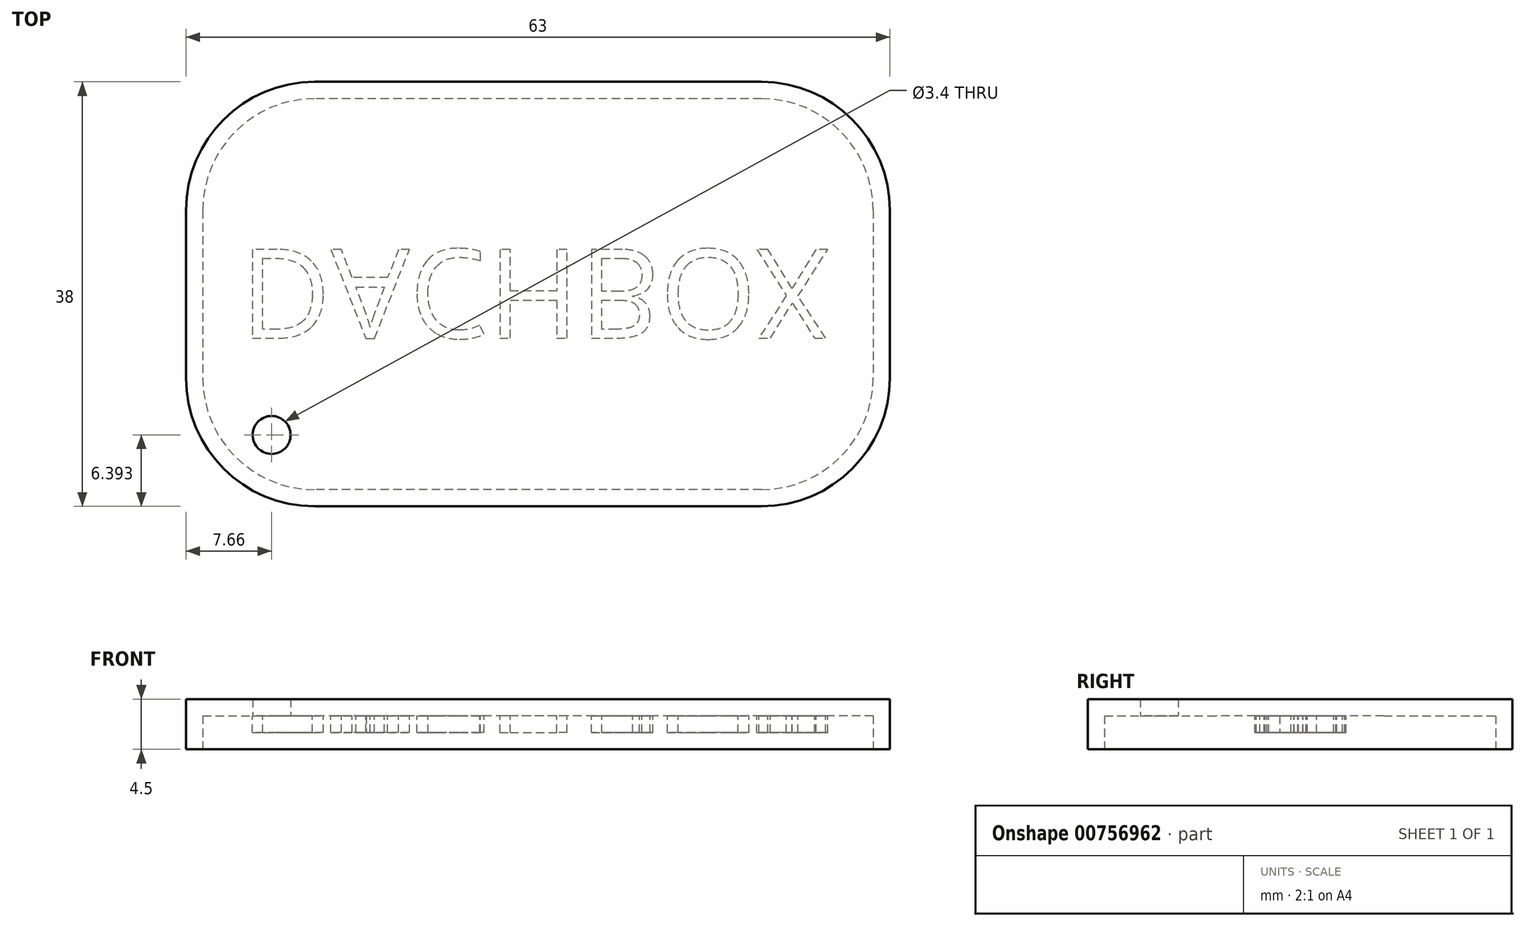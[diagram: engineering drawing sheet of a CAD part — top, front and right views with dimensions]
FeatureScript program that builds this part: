
annotation { "Feature Type Name" : "Feature", "Feature Type Description" : "" }
export const myFeature = defineFeature(function(context is Context, id is Id, definition is map)
    precondition{}
    {
        {
            var Q0;
            Q0=qCreatedBy(makeId("Top.planeOp"),FACE);
            var sketch = newSketch(context, id + "F0", { "sketchPlane" : qUnion([Q0])});
            skLineSegment(sketch, "E0.bottom", {"start": v(30, 17.5) * mm, "end": v(-30, 17.5) * mm});
            skLineSegment(sketch, "E0.top", {"start": v(30, -17.5) * mm, "end": v(-30, -17.5) * mm});
            skLineSegment(sketch, "E0.left", {"start": v(30, 17.5) * mm, "end": v(30, -17.5) * mm});
            skLineSegment(sketch, "E0.right", {"start": v(-30, 17.5) * mm, "end": v(-30, -17.5) * mm});
            skPoint(sketch, "E0.middle", {"position": v(0, 0) * mm});
            skSolve(sketch);
        }
        {
            var Q0;
            Q0=makeQuery(id+"F0.imprint","IMPRINT",FACE,{"disambiguationData":[TD([[makeQuery(id+"F0.imprint","IMPRINT",EDGE,{"derivedFrom":sQuery(id+"F0.wireOp",EDGE,"E0.bottom")}),1.0]])]});
            extrude(context, id + "F1", {"entities" : qUnion([Q0]), "depth" : 3 * mm, "offsetDistance" : 25 * mm});
        }
        {
            var Q0;
            Q0=makeQuery(id+"F1.opExtrude","SWEPT_EDGE",EDGE,{"disambiguationData":[OSD([sQuery(id+"F0.wireOp",EDGE,"E0.bottom"),sQuery(id+"F0.wireOp",EDGE,"E0.left")])]});
            var Q1;
            Q1=makeQuery(id+"F1.opExtrude","SWEPT_EDGE",EDGE,{"disambiguationData":[OSD([sQuery(id+"F0.wireOp",EDGE,"E0.top"),sQuery(id+"F0.wireOp",EDGE,"E0.right")])]});
            var Q2;
            Q2=makeQuery(id+"F1.opExtrude","SWEPT_EDGE",EDGE,{"disambiguationData":[OSD([sQuery(id+"F0.wireOp",EDGE,"E0.top"),sQuery(id+"F0.wireOp",EDGE,"E0.left")])]});
            var Q3;
            Q3=makeQuery(id+"F1.opExtrude","SWEPT_EDGE",EDGE,{"disambiguationData":[OSD([sQuery(id+"F0.wireOp",EDGE,"E0.bottom"),sQuery(id+"F0.wireOp",EDGE,"E0.right")])]});
            fillet(context, id + "F2", {"entities" : qUnion([Q0, Q1, Q2, Q3]), "radius" : 10 * mm, "tangentPropagation" : true, "allowEdgeOverflow" : false});
        }
        {
            var Q0;
            Q0=makeQuery(id+"F1.opExtrude","CAP_FACE",FACE,{"disambiguationData":[OSD([sQuery(id+"F0.wireOp",EDGE,"E0.bottom"),sQuery(id+"F0.wireOp",EDGE,"E0.top"),sQuery(id+"F0.wireOp",EDGE,"E0.left"),sQuery(id+"F0.wireOp",EDGE,"E0.right")])],"isStart":true});
            shell(context, id + "F3", {"entities" : qUnion([Q0]), "thickness" : 1.5 * mm, "oppositeDirection" : true});
        }
        {
            var Q0;
            Q0=makeQuery(id+"F3.opShell","OFFSET_FACE",FACE,{"disambiguationData":[OSD([sQuery(id+"F0.wireOp",EDGE,"E0.bottom"),sQuery(id+"F0.wireOp",EDGE,"E0.top"),sQuery(id+"F0.wireOp",EDGE,"E0.left"),sQuery(id+"F0.wireOp",EDGE,"E0.right")])]});
            var sketch = newSketch(context, id + "F4", { "sketchPlane" : qUnion([Q0])});
            skText(sketch, "E1", { "text": "DACHBOX", "fontName": "OpenSans-Regular.ttf"});
            const initialGuessF4  = {"E1": [-0.02664, -0.004, 1, 0, 0.008]};
            skSetInitialGuess(sketch, initialGuessF4);
            skSolve(sketch);
        }
        {
            var Q0;
            Q0=qSketchRegion(id+"F4",true);
            extrude(context, id + "F5", {"entities" : qUnion([Q0]), "operationType" : NewBodyOperationType.ADD, "depth" : 1.5 * mm, "offsetDistance" : 25 * mm});
        }
        {
            var Q0;
            {var subQ0=sQuery(id+"F0.wireOp",EDGE,"E0.right");var subQ1=sQuery(id+"F0.wireOp",EDGE,"E0.top");var subQ2=sQuery(id+"F0.wireOp",EDGE,"E0.left");var subQ3=sQuery(id+"F0.wireOp",EDGE,"E0.bottom");Q0=makeQuery(id+"F5.boolean.opBoolean","SPLIT",FACE,{"disambiguationData":[TD([makeQuery(id+"F3.opShell","OFFSET_FACE",FACE,{"disambiguationData":[OSD([subQ3])]})])],"derivedFrom":makeQuery(id+"F3.opShell","OFFSET_FACE",FACE,{"disambiguationData":[OSD([subQ3,subQ1,subQ2,subQ0])]})});}
            var sketch = newSketch(context, id + "F6", { "sketchPlane" : qUnion([Q0])});
            skPoint(sketch, "E2", {"position": v(-23.84, 12.6) * mm});
            skSolve(sketch);
        }
        {
            var Q0;
            Q0=sQuery(id+"F6.wireOp",VERTEX,"E2");
            var Q1;
            Q1=makeQuery(id+"F1.opExtrude","SWEPT_BODY",BODY,{"disambiguationData":[OSD([sQuery(id+"F0.wireOp",EDGE,"E0.bottom"),sQuery(id+"F0.wireOp",EDGE,"E0.top"),sQuery(id+"F0.wireOp",EDGE,"E0.left"),sQuery(id+"F0.wireOp",EDGE,"E0.right")])]});
            hole(context, id + "F7", {"style" : HoleStyle.SIMPLE, "endStyle" : HoleEndStyle.THROUGH, "holeDiameter" : 3.4 * mm, "majorDiameter" : 5 * mm, "isTappedThrough" : true, "tappedDepth" : 12 * mm, "tapClearance" : 3, "locations" : qUnion([Q0]), "scope" : qUnion([Q1])});
        }
    });
